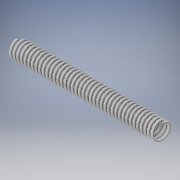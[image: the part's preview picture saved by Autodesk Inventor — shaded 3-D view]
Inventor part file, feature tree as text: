
AUTODESK INVENTOR PART (.ipt)
format: ipt  version: 2018.3 (Build 223284000, 284)  size: 518,656 bytes
history: native  units: in
note: dims shown in document units (in); Inventor stores cm internally (conversion verified against a paired STEP export)
features: helix x1, sketch x1
ambient origin geometry x8: Origin, YZ Plane, XZ Plane, XY Plane, X Axis, Y Axis, Z Axis, Center Point
bodies: Solid1 (feature_tree)
feature tree (2):
  helix  "Coil1"  [1 undecoded]
  sketch  "Sketch1"  dims[d1=0.1035in d2=0.026in d3=1.0in d4=1.7in d5=15.748in d6=0.0in d7=90.0deg d8=90.0deg d9=0.0in d10=0.0in]
note: 1 required parameter value undecoded (feature->parameter linkage not recoverable at this tier; creation-order binding heuristic only, values carry confidence <= 0.55)
